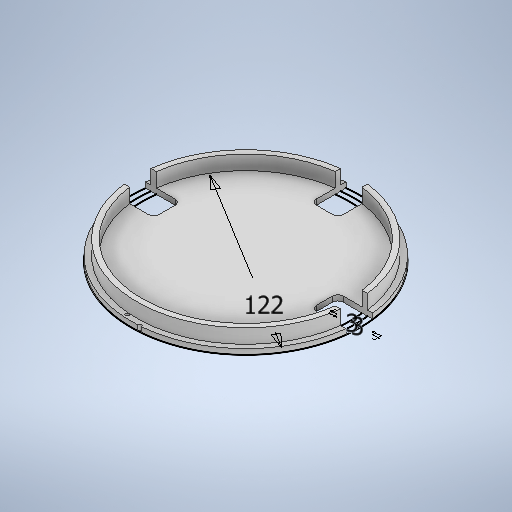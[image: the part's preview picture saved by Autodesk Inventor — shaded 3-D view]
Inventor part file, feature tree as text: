
AUTODESK INVENTOR PART (.ipt)
format: ipt  version: 2025.2 (Build 292293000, 293)  size: 647,168 bytes
history: native  units: in
note: dims shown in document units (in); Inventor stores cm internally (conversion verified against a paired STEP export)
features: extrude x5, sketch x3, pattern_circular x1, fillet x1
ambient origin geometry x8: Origin, YZ Plane, XZ Plane, XY Plane, X Axis, Y Axis, Z Axis, Center Point
bodies: Solid1 (feature_tree)
feature tree (10):
  sketch  "Sketch1"  dims[d0=4.8031in d1=0.1181in]
  extrude  "Extrusion1"  Depth=0.1181in
  extrude  "Extrusion2"  Depth=0.4331in TaperAngle=0.0deg
  extrude  "Extrusion3"  Depth=0.1181in
  extrude  "Extrusion4"  Depth=0.1181in
  extrude  "Extrusion5"  Depth=0.1181in
  pattern_circular  "Circular Pattern1"  [2 undecoded]
  fillet  "Fillet1"  Radius=0.1181in
  sketch  "Sketch2"  dims[d2=0.1181in d3=0.4331in d4=0.0in]
  sketch  "Sketch3"  dims[d5=0.1181in d6=0.0in d7=0.0787in d8=0.1772in d9=0.1772in d10=0.1181in d11=0.0in d12=0.1181in d13=0.0in d14=0.5906in d15=0.7874in d16=0.1181in d17=0.0in d18=1.1811in d19=180.0deg d21=0.1181in]
note: 2 required parameter values undecoded (feature->parameter linkage not recoverable at this tier; creation-order binding heuristic only, values carry confidence <= 0.55)
